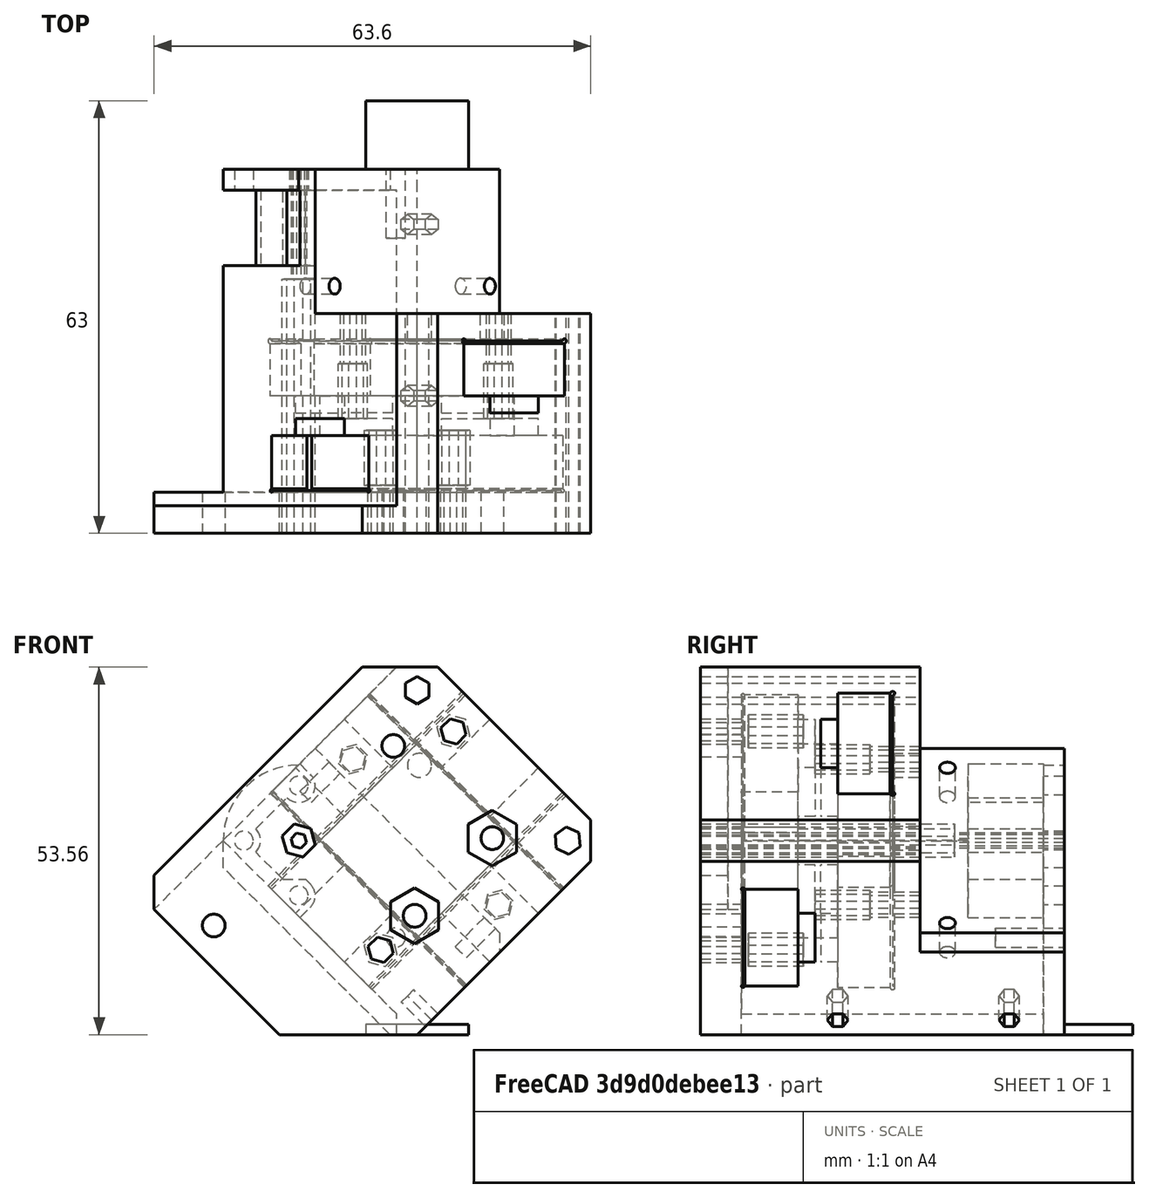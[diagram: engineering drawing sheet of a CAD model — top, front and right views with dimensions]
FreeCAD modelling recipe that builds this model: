
FCSTD DOCUMENT  (FreeCAD 0.19R)
Label: ToolHead_NoScreen_4PocketSplit2Bolts
License: All rights reserved
LicenseURL: http://en.wikipedia.org/wiki/All_rights_reserved
objects: Sketcher::SketchObject×34, PartDesign::Pocket×23, PartDesign::Pad×5, Mesh::Feature×3, PartDesign::Body×1
note: 91 computed .brp shape members not serialized (recipe doc carries the construction recipe); baked Part::Feature solids carry a one-line shape summary decoded from their .brp

FEATURE [Sketcher::SketchObject] Sketch  label="Body001"
  FullyConstrained = true
  MapMode = 5
  Support = -> [XY_Plane]
  sketch-geometry (11):
    g0: LineSegment StartX=20 StartY=15.7574 StartZ=0 EndX=20 EndY=-15.7574 EndZ=0
    g1: LineSegment StartX=15.7574 StartY=-20 StartZ=0 EndX=-20 EndY=-20 EndZ=0
    g2: LineSegment StartX=-20 StartY=-15.7574 StartZ=0 EndX=-20 EndY=19.9515 EndZ=0
    g3: Circle CenterX=-12.1976 CenterY=12.1976 CenterZ=0 NormalX=0 NormalY=0 NormalZ=1 AngleXU=0 Radius=2.1
    g4: LineSegment StartX=-12.1976 StartY=12.1976 StartZ=0 EndX=0 EndY=0 EndZ=0
    g5: ArcOfCircle CenterX=-12.1976 CenterY=12.1976 CenterZ=0 NormalX=0 NormalY=0 NormalZ=1 AngleXU=0 Radius=11 StartAngle=0.788519 EndAngle=2.35931
    g6: LineSegment StartX=-4.44373 StartY=20 StartZ=0 EndX=15.7574 EndY=20 EndZ=0
    g7: LineSegment StartX=15.7574 StartY=-20 StartZ=0 EndX=20 EndY=-15.7574 EndZ=0
    g8: LineSegment StartX=-20 StartY=-15.7574 StartZ=0 EndX=-22.1213 EndY=-17.8787 EndZ=0
    g9: LineSegment StartX=-22.1213 StartY=-17.8787 StartZ=0 EndX=-20 EndY=-20 EndZ=0
    g10: LineSegment StartX=15.7574 StartY=20 StartZ=0 EndX=20 EndY=15.7574 EndZ=0
  constraints (32):
    c: Horizontal(g1)
    c: Vertical(g0)
    c: Vertical(g2)
    c: Distance(g-1,g3) = 17.25
    c: Coincident(g4,g3)
    c: Coincident(g4,g-1)
    c: Angle(g4) = -0.785398
    c: Diameter(g3) = 4.2
    c: Coincident(g5,g3)
    c: Diameter(g5) = 22
    c: DistanceX(g1) = -20
    c: Coincident(g6,g5)
    c: Horizontal(g6)
    c: Coincident(g5,g2)
    c: Coincident(g7,g1)
    c: Coincident(g7,g0)
    c: Angle(g7) = 0.785398
    c: Distance(g7) = 6
    c: DistanceY(g1) = -20
    c: Coincident(g2,g8)
    c: Coincident(g8,g9)
    c: Coincident(g9,g1)
    c: Angle(g9) = -0.785398
    c: Angle(g8) = -2.35619
    c: Distance(g9) = 3
    c: DistanceX(g2) = -20
    c: Coincident(g10,g6)
    c: Coincident(g10,g0)
    c: Distance(g10) = 6
    c: Angle(g10) = -0.785398
    c: DistanceX(g0) = 20
    c: DistanceY(g6) = 20
FEATURE [PartDesign::Pad] Pad
  Direction = (1,1,1)
  Length = 53
  Length2 = 10
  Profile = -> Sketch
  Reversed = true
  Type = 0
FEATURE [Sketcher::SketchObject] Sketch001  label="RailHole"
  FullyConstrained = true
  MapMode = 5
  Placement = pos=(20,0,0) rot=(0.57735,0.57735,0.57735;2.0944rad)
  Support = -> [Pad]
  sketch-geometry (10):
    g0: LineSegment StartX=-10.35 StartY=-27.65 StartZ=0 EndX=-10.35 EndY=-20 EndZ=0
    g1: LineSegment StartX=5 StartY=-17.5 StartZ=0 EndX=-5 EndY=-17.5 EndZ=0
    g2: LineSegment StartX=10 StartY=-28 StartZ=0 EndX=-10 EndY=-28 EndZ=0
    g3: LineSegment StartX=5 StartY=-17.5 StartZ=0 EndX=5 EndY=-20 EndZ=0
    g4: LineSegment StartX=-5 StartY=-20 StartZ=0 EndX=-5 EndY=-17.5 EndZ=0
    g5: LineSegment StartX=-10.35 StartY=-20 StartZ=0 EndX=-5 EndY=-20 EndZ=0
    g6: LineSegment StartX=5 StartY=-20 StartZ=0 EndX=10.3495 EndY=-20 EndZ=0
    g7: LineSegment StartX=10.3495 StartY=-27.65 StartZ=0 EndX=10.3495 EndY=-20 EndZ=0
    g8: ArcOfCircle CenterX=-10.35 CenterY=-28 CenterZ=0 NormalX=0 NormalY=0 NormalZ=1 AngleXU=0 Radius=0.35 StartAngle=1.5708 EndAngle=6.28319
    g9: ArcOfCircle CenterX=10.35 CenterY=-28 CenterZ=0 NormalX=0 NormalY=0 NormalZ=1 AngleXU=0 Radius=0.35 StartAngle=3.14159 EndAngle=7.85541
  constraints (29):
    c: Vertical(g0)
    c: Symmetric(g1,g1,g-2)
    c: Distance(g1) = 10
    c: Coincident(g1,g3)
    c: Vertical(g3)
    c: Coincident(g4,g1)
    c: Symmetric(g3,g4,g-2)
    c: Distance(g3) = 2.5
    c: Distance(g2) = 20
    c: Coincident(g5,g4)
    c: Horizontal(g5)
    c: Coincident(g3,g6)
    c: Horizontal(g6)
    c: Vertical(g7)
    c: Coincident(g0,g5)
    c: Coincident(g7,g6)
    c: Coincident(g0,g8)
    c: Coincident(g8,g2)
    c: Diameter(g8) = 0.7
    c: DistanceX(g0,g8) = 0
    c: DistanceY(g2,g8) = 0
    c: Coincident(g9,g2)
    c: Coincident(g9,g7)
    c: Diameter(g9) = 0.7
    c: DistanceY(g2,g9) = 0
    c: DistanceX(g7,g9) = 0.0005
    c: Symmetric(g9,g8,g-2)
    c: Distance(g9,g6) = 8
    c: DistanceY(g8) = -28
FEATURE [PartDesign::Pocket] Pocket
  BaseFeature = -> Pad
  Length = 5
  Length2 = 100
  Profile = -> Sketch001
  Type = 1
FEATURE [Sketcher::SketchObject] Sketch008  label="ExtruderHole"
  FullyConstrained = false
  MapMode = 5
  Placement = pos=(0,0,4) rot=(0,0,1;0rad)
  sketch-geometry (2):
    g0: LineSegment StartX=0 StartY=0 StartZ=0 EndX=-54.6242 EndY=54.6242 EndZ=0
    g1: Circle CenterX=-12.1976 CenterY=12.1976 CenterZ=0 NormalX=0 NormalY=0 NormalZ=1 AngleXU=0 Radius=0.75
  constraints (5):
    c: Coincident(g0,g-1)
    c: Angle(g0) = 2.35619
    c: PointOnObject(g1,g0)
    c: Distance(g-1,g1) = 17.25
    c: Diameter(g1) = 1.5
FEATURE [Sketcher::SketchObject] Sketch009  label="reference"
  FullyConstrained = false
  MapMode = 5
  Placement = pos=(0,0,-25) rot=(1,0,0;3.14159rad)
  sketch-geometry (2):
    g0: Circle CenterX=-12.0208 CenterY=-12.0208 CenterZ=0 NormalX=0 NormalY=0 NormalZ=1 AngleXU=0 Radius=10
    g1: LineSegment StartX=0 StartY=0 StartZ=0 EndX=-27.7674 EndY=-27.7674 EndZ=0
  constraints (5):
    c: Diameter(g0) = 20
    c: Coincident(g1,g-1)
    c: Angle(g1) = -2.35619
    c: PointOnObject(g0,g1)
    c: Distance(g0,g1) = 17
FEATURE [Sketcher::SketchObject] Sketch010  label="reference2"
  FullyConstrained = false
  MapMode = 5
  Placement = pos=(0,0,-37) rot=(1,0,0;3.14159rad)
  sketch-geometry (2):
    g0: Circle CenterX=-12.1976 CenterY=-12.1976 CenterZ=0 NormalX=0 NormalY=0 NormalZ=1 AngleXU=0 Radius=8
    g1: LineSegment StartX=0 StartY=0 StartZ=0 EndX=-38.1566 EndY=-38.1566 EndZ=0
  constraints (5):
    c: Diameter(g0) = 16
    c: Coincident(g1,g-1)
    c: Angle(g1) = -2.35619
    c: Distance(g0,g1) = 17.25
    c: PointOnObject(g0,g1)
FEATURE [Sketcher::SketchObject] Sketch021  label="InternalTri"
  FullyConstrained = true
  MapMode = 5
  Placement = pos=(0,-3e-15,-12) rot=(0,0,1;0rad)
  sketch-geometry (4):
    g0: LineSegment StartX=-10 StartY=10 StartZ=0 EndX=10 EndY=10 EndZ=0
    g1: LineSegment StartX=10 StartY=10 StartZ=0 EndX=10 EndY=-10 EndZ=0
    g2: LineSegment StartX=10 StartY=-10 StartZ=0 EndX=-10 EndY=-10 EndZ=0
    g3: LineSegment StartX=-10 StartY=-10 StartZ=0 EndX=-10 EndY=10 EndZ=0
  constraints (11):
    c: Coincident(g0,g1)
    c: Coincident(g1,g2)
    c: Coincident(g2,g3)
    c: Coincident(g3,g0)
    c: Horizontal(g0)
    c: Horizontal(g2)
    c: Vertical(g1)
    c: Vertical(g3)
    c: Symmetric(g1,g0,g-1)
    c: Equal(g1,g0)
    c: Distance(g1) = 20
FEATURE [PartDesign::Pocket] Pocket002
  BaseFeature = -> Pocket
  Length = 10
  Length2 = 2
  Profile = -> Sketch021
  Type = 4
FEATURE [Sketcher::SketchObject] Sketch019  label="RailHole2"
  FullyConstrained = true
  MapMode = 5
  Placement = pos=(0,-20,0) rot=(1,0,0;1.5708rad)
  Support = -> [Pocket002]
  sketch-geometry (10):
    g0: LineSegment StartX=-9.75 StartY=-6.2 StartZ=0 EndX=9.75 EndY=-6.2 EndZ=0
    g1: LineSegment StartX=10 StartY=-14.2 StartZ=0 EndX=5 EndY=-14.2 EndZ=0
    g2: LineSegment StartX=5 StartY=-14.2 StartZ=0 EndX=5 EndY=-16.7 EndZ=0
    g3: LineSegment StartX=5 StartY=-16.7 StartZ=0 EndX=-5 EndY=-16.7 EndZ=0
    g4: LineSegment StartX=-5 StartY=-16.7 StartZ=0 EndX=-5 EndY=-14.2 EndZ=0
    g5: LineSegment StartX=-5 StartY=-14.2 StartZ=0 EndX=-10 EndY=-14.2 EndZ=0
    g6: ArcOfCircle CenterX=10 CenterY=-6.2 CenterZ=0 NormalX=0 NormalY=0 NormalZ=1 AngleXU=0 Radius=0.25 StartAngle=4.71239 EndAngle=9.42478
    g7: ArcOfCircle CenterX=-10 CenterY=-6.2 CenterZ=0 NormalX=0 NormalY=0 NormalZ=1 AngleXU=0 Radius=0.25 StartAngle=-9e-16 EndAngle=4.71239
    g8: LineSegment StartX=-10 StartY=-14.2 StartZ=0 EndX=-10 EndY=-6.45 EndZ=0
    g9: LineSegment StartX=10 StartY=-14.2 StartZ=0 EndX=10 EndY=-6.45 EndZ=0
  constraints (29):
    c: Horizontal(g0)
    c: Horizontal(g1)
    c: Coincident(g1,g2)
    c: Vertical(g2)
    c: Coincident(g2,g3)
    c: Horizontal(g3)
    c: Coincident(g3,g4)
    c: Vertical(g4)
    c: Coincident(g4,g5)
    c: Symmetric(g1,g5,g-2)
    c: Distance(g3) = 10
    c: Symmetric(g4,g1,g-2)
    c: DistanceY(g0) = -6.2
    c: Distance(g2) = 2.5
    c: Coincident(g6,g0)
    c: Coincident(g7,g0)
    c: Distance(g7,g6) = 20
    c: DistanceY(g1,g6) = 8
    c: Coincident(g8,g5)
    c: Vertical(g8)
    c: Coincident(g9,g1)
    c: Coincident(g9,g6)
    c: Vertical(g9)
    c: Coincident(g7,g8)
    c: Symmetric(g6,g7,g-2)
    c: Diameter(g6) = 0.5
    c: Equal(g6,g7)
    c: DistanceX(g7,g7) = 0
    c: DistanceY(g7,g0) = 0
FEATURE [Sketcher::SketchObject] Sketch024  label="hgxLITEholes"
  FullyConstrained = false
  MapMode = 5
  Placement = pos=(0,0,4) rot=(0,0,1;0rad)
  sketch-geometry (5):
    g0: Circle CenterX=7.3 CenterY=12.2 CenterZ=0 NormalX=0 NormalY=0 NormalZ=1 AngleXU=0 Radius=1.65
    g1: Circle CenterX=-29.7 CenterY=12.2 CenterZ=0 NormalX=0 NormalY=0 NormalZ=1 AngleXU=0 Radius=1.65
    g2: LineSegment StartX=-29.7 StartY=12.2 StartZ=0 EndX=7.3 EndY=12.2 EndZ=0
    g3: LineSegment StartX=0 StartY=0 StartZ=0 EndX=-27.1729 EndY=27.1729 EndZ=0
    g4: Circle CenterX=-12.2 CenterY=12.2 CenterZ=0 NormalX=0 NormalY=0 NormalZ=1 AngleXU=0 Radius=1.0154
  constraints (12):
    c: Diameter(g0) = 3.3
    c: Equal(g0,g1)
    c: Coincident(g2,g1)
    c: Coincident(g2,g0)
    c: Distance(g2) = 37
    c: Coincident(g3,g-1)
    c: Angle(g3) = 2.35619
    c: PointOnObject(g4,g3)
    c: Distance(g4,g0) = 19.5
    c: Horizontal(g2)
    c: PointOnObject(g4,g2)
    c: DistanceY(g4) = 12.2
FEATURE [PartDesign::Pocket] Pocket003
  BaseFeature = -> Pocket002
  Length = 5
  Length2 = 100
  Profile = -> Sketch019
  Type = 1
FEATURE [Sketcher::SketchObject] Sketch026  label="BottomSculp"
  FullyConstrained = false
  MapMode = 5
  Placement = pos=(0,0,-53) rot=(1,0,0;3.14159rad)
  Support = -> [Pocket003]
  sketch-geometry (5):
    g0: LineSegment StartX=29.4648 StartY=27.8981 StartZ=0 EndX=28.2209 EndY=-23.4245 EndZ=0
    g1: LineSegment StartX=28.2209 StartY=-23.4245 StartZ=0 EndX=-1.00001 EndY=-23.4245 EndZ=0
    g2: LineSegment StartX=-1.00001 StartY=-23.4245 StartZ=0 EndX=-1 EndY=18 EndZ=0
    g3: LineSegment StartX=-1 StartY=18 StartZ=0 EndX=-14.2089 EndY=31.2089 EndZ=0
    g4: LineSegment StartX=-14.2089 StartY=31.2089 StartZ=0 EndX=29.4648 EndY=27.8981 EndZ=0
  constraints (11):
    c: Coincident(g0,g1)
    c: Horizontal(g1)
    c: Coincident(g1,g2)
    c: Angle(g2) = 1.5708
    c: Coincident(g2,g3)
    c: Angle(g3) = 2.35619
    c: Coincident(g4,g3)
    c: Coincident(g4,g0)
    c: DistanceY(g2) = 18
    c: DistanceX(g2) = -1
    c: Angle(g3) = 2.35619
FEATURE [PartDesign::Pocket] Pocket004
  BaseFeature = -> Pocket003
  Length = 21
  Length2 = 100
  Profile = -> Sketch026
  Type = 0
FEATURE [Sketcher::SketchObject] Sketch004  label="Yboltpattern"
  FullyConstrained = true
  MapMode = 5
  Placement = pos=(0,0,-32) rot=(1,0,0;3.14159rad)
  Support = -> [Pocket004]
  sketch-geometry (8):
    g0: Circle CenterX=-8 CenterY=7.5 CenterZ=0 NormalX=0 NormalY=0 NormalZ=1 AngleXU=0 Radius=1.75
    g1: Circle CenterX=8 CenterY=7.5 CenterZ=0 NormalX=0 NormalY=0 NormalZ=1 AngleXU=0 Radius=1.75
    g2: Circle CenterX=-8 CenterY=-7.5 CenterZ=0 NormalX=0 NormalY=0 NormalZ=1 AngleXU=0 Radius=1.75
    g3: Circle CenterX=8 CenterY=-7.5 CenterZ=0 NormalX=0 NormalY=0 NormalZ=1 AngleXU=0 Radius=1.75
    g4: LineSegment StartX=-8 StartY=7.5 StartZ=0 EndX=8 EndY=7.5 EndZ=0
    g5: LineSegment StartX=8 StartY=7.5 StartZ=0 EndX=8 EndY=-7.5 EndZ=0
    g6: LineSegment StartX=8 StartY=-7.5 StartZ=0 EndX=-8 EndY=-7.5 EndZ=0
    g7: LineSegment StartX=-8 StartY=-7.5 StartZ=0 EndX=-8 EndY=7.5 EndZ=0
  constraints (18):
    c: Diameter(g0) = 3.5
    c: Equal(g0,g1)
    c: Equal(g0,g2)
    c: Equal(g0,g3)
    c: Distance(g2,g0) = 15
    c: Distance(g3,g2) = 16
    c: Coincident(g4,g0)
    c: Coincident(g4,g1)
    c: Coincident(g4,g5)
    c: Coincident(g5,g3)
    c: Coincident(g5,g6)
    c: Coincident(g6,g2)
    c: Coincident(g6,g7)
    c: Coincident(g7,g4)
    c: Equal(g5,g7)
    c: Equal(g4,g6)
    c: Symmetric(g1,g2,g-1)
    c: Symmetric(g0,g1,g-2)
FEATURE [Sketcher::SketchObject] Sketch022  label="VoronHoleRelif"
  FullyConstrained = true
  MapMode = 5
  Placement = pos=(0,0,-28) rot=(0,0,1;0rad)
  Support = -> [Pocket004]
  sketch-geometry (11):
    g0: ArcOfCircle CenterX=-17.8884 CenterY=6.52425 CenterZ=0 NormalX=0 NormalY=0 NormalZ=1 AngleXU=0 Radius=2.4 StartAngle=4.71239 EndAngle=6.28319
    g1: ArcOfCircle CenterX=-6.58192 CenterY=17.8307 CenterZ=0 NormalX=0 NormalY=0 NormalZ=1 AngleXU=0 Radius=2.4 StartAngle=3.14159 EndAngle=6.28319
    g2: LineSegment StartX=-22.2684 StartY=4.12425 StartZ=0 EndX=-17.8884 EndY=4.12425 EndZ=0
    g3: LineSegment StartX=-22.2684 StartY=23.8307 StartZ=0 EndX=-4.18192 EndY=23.8307 EndZ=0
    g4: LineSegment StartX=-4.18192 StartY=23.8307 StartZ=0 EndX=-4.18192 EndY=17.8307 EndZ=0
    g5: LineSegment StartX=-22.2684 StartY=4.12425 StartZ=0 EndX=-22.2684 EndY=23.8307 EndZ=0
    g6: ArcOfCircle CenterX=-17.8172 CenterY=17.8307 CenterZ=0 NormalX=0 NormalY=0 NormalZ=1 AngleXU=0 Radius=2.4 StartAngle=4.71239 EndAngle=6.28319
    g7: LineSegment StartX=-15.4172 StartY=17.8307 StartZ=0 EndX=-8.98192 EndY=17.8307 EndZ=0
    g8: LineSegment StartX=-17.8172 StartY=9.85307 StartZ=0 EndX=-15.4884 EndY=7.52425 EndZ=0
    g9: LineSegment StartX=-15.4884 StartY=6.52425 StartZ=0 EndX=-15.4884 EndY=7.52425 EndZ=0
    g10: LineSegment StartX=-17.8172 StartY=9.85307 StartZ=0 EndX=-17.8172 EndY=15.4307 EndZ=0
  constraints (33):
    c: Horizontal(g2)
    c: Coincident(g3,g4)
    c: Tangent(g4,g1) = 1.5708
    c: Tangent(g2,g0) = -1.5708
    c: Diameter(g0) = 4.8
    c: Equal(g0,g1)
    c: Vertical(g4)
    c: Horizontal(g3)
    c: Coincident(g5,g2)
    c: Coincident(g5,g3)
    c: Vertical(g5)
    c: Distance(g2) = 4.38
    c: Distance(g4) = 6
    c: DistanceX(g1) = -6.58192
    c: DistanceY(g1) = 17.8307
    c: DistanceX(g0) = -17.8884
    c: DistanceY(g0) = 6.52425
    c: Coincident(g7,g6)
    c: Coincident(g7,g1)
    c: Horizontal(g7)
    c: Perpendicular(g1,g7)
    c: Diameter(g6) = 4.8
    c: Perpendicular(g6,g7)
    c: Angle(g8) = -0.785398
    c: Vertical(g9)
    c: Tangent(g9,g0) = -1.5708
    c: Distance(g9) = 1
    c: Coincident(g8,g9)
    c: Coincident(g10,g8)
    c: Coincident(g10,g6)
    c: Vertical(g10)
    c: Perpendicular(g6,g10)
    c: DistanceX(g6) = -17.8172
FEATURE [PartDesign::Pocket] Pocket005
  BaseFeature = -> Pocket004
  Length = 22
  Length2 = -11
  Profile = -> Sketch022
  Type = 4
FEATURE [Sketcher::SketchObject] Sketch017  label="VoronHoles3"
  FullyConstrained = true
  MapMode = 5
  Placement = pos=(0,0,-50) rot=(0,0,1;0rad)
  Support = -> [Pocket005]
  sketch-geometry (10):
    g0: Circle CenterX=-6.54074 CenterY=17.8544 CenterZ=0 NormalX=0 NormalY=0 NormalZ=1 AngleXU=0 Radius=1.375
    g1: Circle CenterX=-17.8544 CenterY=6.54074 CenterZ=0 NormalX=0 NormalY=0 NormalZ=1 AngleXU=0 Radius=1.375
    g2: Circle CenterX=-6.54074 CenterY=6.54074 CenterZ=0 NormalX=0 NormalY=0 NormalZ=1 AngleXU=0 Radius=1.375
    g3: Circle CenterX=-17.8544 CenterY=17.8544 CenterZ=0 NormalX=0 NormalY=0 NormalZ=1 AngleXU=0 Radius=1.375
    g4: LineSegment StartX=-6.54074 StartY=17.8544 StartZ=0 EndX=-6.54074 EndY=6.54074 EndZ=0
    g5: LineSegment StartX=-6.54074 StartY=6.54074 StartZ=0 EndX=-17.8544 EndY=6.54074 EndZ=0
    g6: LineSegment StartX=-17.8544 StartY=6.54074 StartZ=0 EndX=-17.8544 EndY=17.8544 EndZ=0
    g7: LineSegment StartX=-17.8544 StartY=17.8544 StartZ=0 EndX=-6.54074 EndY=17.8544 EndZ=0
    g8: LineSegment StartX=0 StartY=0 StartZ=0 EndX=-37.1726 EndY=37.1726 EndZ=0
    g9: Circle CenterX=-12.1976 CenterY=12.1976 CenterZ=0 NormalX=0 NormalY=0 NormalZ=1 AngleXU=0 Radius=0.77
  constraints (25):
    c: Coincident(g4,g0)
    c: Coincident(g4,g2)
    c: Coincident(g4,g5)
    c: Coincident(g5,g1)
    c: Coincident(g5,g6)
    c: Coincident(g6,g3)
    c: Coincident(g6,g7)
    c: Coincident(g7,g4)
    c: Equal(g4,g7)
    c: Equal(g7,g6)
    c: Equal(g6,g5)
    c: Coincident(g8,g-1)
    c: PointOnObject(g9,g8)
    c: Distance(g-1,g9) = 17.25
    c: Diameter(g1) = 2.75
    c: Equal(g1,g3)
    c: Equal(g1,g0)
    c: Equal(g1,g2)
    c: Symmetric(g0,g1,g9)
    c: Distance(g2,g3) = 16
    c: Angle(g8) = 2.35619
    c: PointOnObject(g2,g8)
    c: Perpendicular(g7,g4)
    c: Distance(g8) = 52.57
    c: Diameter(g9) = 1.54
FEATURE [PartDesign::Pocket] Pocket006
  BaseFeature = -> Pocket005
  Length = 5
  Length2 = 100
  Profile = -> Sketch017
  Type = 1
FEATURE [Sketcher::SketchObject] Sketch025  label="FanDuctMountHole"
  FullyConstrained = true
  MapMode = 5
  Placement = pos=(0,0,-53) rot=(1,0,0;3.14159rad)
  Support = -> [Pocket006]
  sketch-geometry (1):
    g0: Circle CenterX=-12.2 CenterY=7.8 CenterZ=0 NormalX=0 NormalY=0 NormalZ=1 AngleXU=0 Radius=1.4
  constraints (3):
    c: Diameter(g0) = 2.8
    c: DistanceX(g0) = -12.2
    c: DistanceY(g0) = 7.8
FEATURE [PartDesign::Pocket] Pocket007
  BaseFeature = -> Pocket006
  Length = 10
  Length2 = 100
  Profile = -> Sketch025
  Type = 0
FEATURE [PartDesign::Pocket] Pocket008
  BaseFeature = -> Pocket007
  Length = 9
  Length2 = 100
  Profile = -> Sketch004
  Type = 0
FEATURE [Sketcher::SketchObject] Sketch007  label="ExtruderPlatform"
  ExternalGeometry = -> [Pad]
  FullyConstrained = false
  MapMode = 5
  Support = -> [Pocket008]
  sketch-geometry (12):
    g0: LineSegment StartX=-20 StartY=-20 StartZ=0 EndX=15.7574 EndY=-20 EndZ=0
    g1: LineSegment StartX=0 StartY=0 StartZ=0 EndX=-70.7107 EndY=70.7107 EndZ=0
    g2: Circle CenterX=-12.1976 CenterY=12.1976 CenterZ=0 NormalX=0 NormalY=0 NormalZ=1 AngleXU=0 Radius=2.125
    g3: LineSegment StartX=15.7574 StartY=-20 StartZ=0 EndX=20 EndY=-15.7574 EndZ=0
    g4: LineSegment StartX=20 StartY=-15.7574 StartZ=0 EndX=20 EndY=15.7574 EndZ=0
    g5: LineSegment StartX=20 StartY=15.7574 StartZ=0 EndX=15.7574 EndY=20 EndZ=0
    g6: LineSegment StartX=-20 StartY=-20 StartZ=0 EndX=-34.1976 EndY=-5.80241 EndZ=0
    g7: LineSegment StartX=-12.1976 StartY=-100 StartZ=0 EndX=-12.1976 EndY=100 EndZ=0
    g8: LineSegment StartX=-34.1976 StartY=-5.80241 StartZ=0 EndX=-34.1976 EndY=20 EndZ=0
    g9: LineSegment StartX=-34.1976 StartY=20 StartZ=0 EndX=15.7574 EndY=20 EndZ=0
    g10: Circle CenterX=-29.6976 CenterY=12.1976 CenterZ=0 NormalX=0 NormalY=0 NormalZ=1 AngleXU=0 Radius=1.4
    g11: Circle CenterX=7.30241 CenterY=11.9057 CenterZ=0 NormalX=0 NormalY=0 NormalZ=1 AngleXU=0 Radius=1.4
  constraints (35):
    c: Coincident(g1,g-1)
    c: Angle(g1) = 2.35619
    c: Diameter(g2) = 4.25
    c: PointOnObject(g2,g1)
    c: Distance(g-1,g2) = 17.25
    c: Coincident(g0,g3)
    c: Coincident(g3,g4)
    c: Coincident(g6,g0)
    c: Angle(g6) = 2.35619
    c: Coincident(g5,g4)
    c: Distance(g1) = 100
    c: PointOnObject(g2,g7)
    c: DistanceX(g0,g0) = -35.7574
    c: DistanceY(g0,g0) = 0
    c: DistanceX(g3,g0) = -40
    c: DistanceY(g3,g0) = -4.24264
    c: DistanceX(g4) = 20
    c: DistanceY(g4) = 15.7574
    c: DistanceX(g3) = 20
    c: DistanceY(g3) = -15.7574
    c: Coincident(g8,g6)
    c: Vertical(g8)
    c: Horizontal(g9)
    c: Coincident(g5,g9)
    c: Distance(g8,g7) = 22
    c: DistanceX(g5) = 15.7574
    c: DistanceY(g5) = 20
    c: Symmetric(g7,g7,g-1)
    c: Distance(g7) = 200
    c: DistanceX(g10,g2) = 17.5
    c: DistanceX(g2,g11) = 19.5
    c: Diameter(g10) = 2.8
    c: Equal(g10,g11)
    c: DistanceY(g10,g2) = 0
    c: Coincident(g9,g8)
FEATURE [PartDesign::Pad] Pad001
  BaseFeature = -> Pocket008
  Direction = (1,1,1)
  Length = 6
  Length2 = 100
  Profile = -> Sketch007
  Reversed = true
  Type = 0
FEATURE [PartDesign::Pocket] Pocket009
  BaseFeature = -> Pad001
  Length = 11
  Length2 = 100
  Profile = -> Sketch024
  Type = 0
FEATURE [PartDesign::Pocket] Pocket010
  BaseFeature = -> Pocket009
  Length = 5
  Length2 = 100
  Profile = -> Sketch008
  Type = 1
FEATURE [Sketcher::SketchObject] Sketch003  label="Xboltpattern"
  FullyConstrained = true
  MapMode = 5
  Support = -> [Pocket010]
  sketch-geometry (8):
    g0: Circle CenterX=-8 CenterY=7.5 CenterZ=0 NormalX=0 NormalY=0 NormalZ=1 AngleXU=0 Radius=1.65
    g1: Circle CenterX=8 CenterY=7.5 CenterZ=0 NormalX=0 NormalY=0 NormalZ=1 AngleXU=0 Radius=1.65
    g2: Circle CenterX=-8 CenterY=-7.5 CenterZ=0 NormalX=0 NormalY=0 NormalZ=1 AngleXU=0 Radius=1.65
    g3: Circle CenterX=8 CenterY=-7.5 CenterZ=0 NormalX=0 NormalY=0 NormalZ=1 AngleXU=0 Radius=1.65
    g4: LineSegment StartX=-8 StartY=7.5 StartZ=0 EndX=8 EndY=7.5 EndZ=0
    g5: LineSegment StartX=8 StartY=7.5 StartZ=0 EndX=8 EndY=-7.5 EndZ=0
    g6: LineSegment StartX=8 StartY=-7.5 StartZ=0 EndX=-8 EndY=-7.5 EndZ=0
    g7: LineSegment StartX=-8 StartY=-7.5 StartZ=0 EndX=-8 EndY=7.5 EndZ=0
  constraints (19):
    c: Diameter(g0) = 3.3
    c: Equal(g0,g1)
    c: Equal(g0,g2)
    c: Equal(g0,g3)
    c: Distance(g0,g1) = 16
    c: Distance(g1,g3) = 15
    c: Coincident(g4,g0)
    c: Coincident(g4,g1)
    c: Horizontal(g4)
    c: Coincident(g4,g5)
    c: Coincident(g5,g3)
    c: Vertical(g5)
    c: Coincident(g5,g6)
    c: Coincident(g6,g2)
    c: Coincident(g6,g7)
    c: Coincident(g7,g4)
    c: Symmetric(g2,g1,g-1)
    c: Equal(g7,g5)
    c: Equal(g6,g4)
FEATURE [Sketcher::SketchObject] Sketch029  label="Adhesion"
  FullyConstrained = false
  MapMode = 5
  Placement = pos=(0,0,-53) rot=(1,0,0;3.14159rad)
  sketch-geometry (4):
    g0: LineSegment StartX=-13.636 StartY=24.2426 StartZ=0 EndX=-24.2426 EndY=13.636 EndZ=0
    g1: LineSegment StartX=-24.2426 StartY=13.636 StartZ=0 EndX=-25.3033 EndY=14.6967 EndZ=0
    g2: LineSegment StartX=-25.3033 StartY=14.6967 StartZ=0 EndX=-14.6967 EndY=25.3033 EndZ=0
    g3: LineSegment StartX=-14.6967 StartY=25.3033 StartZ=0 EndX=-13.636 EndY=24.2426 EndZ=0
  constraints (10):
    c: Coincident(g0,g1)
    c: Coincident(g1,g2)
    c: Coincident(g2,g3)
    c: Coincident(g3,g0)
    c: Angle(g2) = 0.785398
    c: Distance(g2) = 15
    c: Distance(g1) = 1.5
    c: Distance(g3) = 1.5
    c: Perpendicular(g2,g3)
    c: Perpendicular(g2,g1)
FEATURE [Sketcher::SketchObject] Sketch033  label="WireMgmnt"
  FullyConstrained = true
  MapMode = 5
  Placement = pos=(0,-20,0) rot=(1,0,0;1.5708rad)
  sketch-geometry (14):
    g0: LineSegment StartX=-15.7 StartY=-20.7506 StartZ=0 EndX=-15.7 EndY=-19.2494 EndZ=0
    g1: LineSegment StartX=-15.7 StartY=-19.2494 StartZ=0 EndX=-17 EndY=-18.4989 EndZ=0
    g2: LineSegment StartX=-17 StartY=-18.4989 StartZ=0 EndX=-18.3 EndY=-19.2494 EndZ=0
    g3: LineSegment StartX=-18.3 StartY=-19.2494 StartZ=0 EndX=-18.3 EndY=-20.7506 EndZ=0
    g4: LineSegment StartX=-18.3 StartY=-20.7506 StartZ=0 EndX=-17 EndY=-21.5011 EndZ=0
    g5: LineSegment StartX=-17 StartY=-21.5011 StartZ=0 EndX=-15.7 EndY=-20.7506 EndZ=0
    g6: Circle CenterX=-17 CenterY=-20 CenterZ=0 NormalX=0 NormalY=0 NormalZ=1 AngleXU=0 Radius=1.50111
    g7: LineSegment StartX=-15.7 StartY=-44.2494 StartZ=0 EndX=-17 EndY=-43.4989 EndZ=0
    g8: LineSegment StartX=-17 StartY=-43.4989 StartZ=0 EndX=-18.3 EndY=-44.2494 EndZ=0
    g9: LineSegment StartX=-18.3 StartY=-44.2494 StartZ=0 EndX=-18.3 EndY=-45.7506 EndZ=0
    g10: LineSegment StartX=-18.3 StartY=-45.7506 StartZ=0 EndX=-17 EndY=-46.5011 EndZ=0
    g11: LineSegment StartX=-17 StartY=-46.5011 StartZ=0 EndX=-15.7 EndY=-45.7506 EndZ=0
    g12: LineSegment StartX=-15.7 StartY=-45.7506 StartZ=0 EndX=-15.7 EndY=-44.2494 EndZ=0
    g13: Circle CenterX=-17 CenterY=-45 CenterZ=0 NormalX=0 NormalY=0 NormalZ=1 AngleXU=0 Radius=1.50111
  constraints (34):
    c: Coincident(g0,g1)
    c: Coincident(g1,g2)
    c: Coincident(g2,g3)
    c: Coincident(g3,g4)
    c: Coincident(g4,g5)
    c: Coincident(g5,g0)
    c: Equal(g0, g1-g5) x5
    c: PointOnObject(g0,g6)
    c: PointOnObject(g1,g6)
    c: PointOnObject(g2,g6)
    c: PointOnObject(g3,g6)
    c: PointOnObject(g4,g6)
    c: PointOnObject(g5,g6)
    c: Coincident(g7,g8)
    c: Coincident(g8,g9)
    c: Coincident(g9,g10)
    c: Coincident(g10,g11)
    c: Coincident(g11,g12)
    c: Coincident(g12,g7)
    c: Equal(g7, g8-g12) x5
    c: PointOnObject(g7,g13)
    c: PointOnObject(g8,g13)
    c: PointOnObject(g9,g13)
    c: PointOnObject(g10,g13)
    c: PointOnObject(g11,g13)
    c: PointOnObject(g12,g13)
    c: DistanceX(g13) = -17
    c: Distance(g10,g7) = 2.6
    c: Vertical(g9)
    c: DistanceY(g13) = -45
    c: Distance(g3,g0) = 2.6
    c: DistanceY(g6) = -20
    c: Vertical(g3)
    c: DistanceX(g6) = -17
FEATURE [Sketcher::SketchObject] Sketch035  label="Bottom Reinforce"
  FullyConstrained = false
  MapMode = 5
  Placement = pos=(0,0,-53) rot=(1,0,0;3.14159rad)
  sketch-geometry (4):
    g0: LineSegment StartX=-22.779 StartY=17.221 StartZ=0 EndX=-22.779 EndY=-17.1725 EndZ=0
    g1: LineSegment StartX=-22.779 StartY=-17.1725 StartZ=0 EndX=-20 EndY=-19.9515 EndZ=0
    g2: LineSegment StartX=-20 StartY=-19.9515 StartZ=0 EndX=-20 EndY=20 EndZ=0
    g3: LineSegment StartX=-20 StartY=20 StartZ=0 EndX=-22.779 EndY=17.221 EndZ=0
  constraints (9):
    c: Vertical(g0)
    c: Coincident(g0,g1)
    c: Coincident(g1,g2)
    c: Vertical(g2)
    c: Coincident(g2,g3)
    c: Coincident(g3,g0)
    c: Angle(g1) = -0.785398
    c: DistanceY(g2) = 20
    c: Angle(g3) = -2.35619
FEATURE [Sketcher::SketchObject] Sketch037  label="BumpTrim"
  FullyConstrained = false
  MapMode = 5
  sketch-geometry (4):
    g0: LineSegment StartX=-26.2848 StartY=31.2083 StartZ=0 EndX=-1.26106 EndY=31.2083 EndZ=0
    g1: LineSegment StartX=-1.26106 StartY=31.2083 StartZ=0 EndX=-1.26106 EndY=20 EndZ=0
    g2: LineSegment StartX=-1.26106 StartY=20 StartZ=0 EndX=-26.2848 EndY=20 EndZ=0
    g3: LineSegment StartX=-26.2848 StartY=20 StartZ=0 EndX=-26.2848 EndY=31.2083 EndZ=0
  constraints (9):
    c: Coincident(g0,g1)
    c: Coincident(g1,g2)
    c: Coincident(g2,g3)
    c: Coincident(g3,g0)
    c: Horizontal(g0)
    c: Horizontal(g2)
    c: Vertical(g1)
    c: Vertical(g3)
    c: DistanceY(g1) = 20
FEATURE [PartDesign::Pocket] Pocket011
  BaseFeature = -> Pocket010
  Length = 10
  Length2 = 100
  Profile = -> Sketch003
  Type = 0
FEATURE [Sketcher::SketchObject] Sketch036  label="countersink"
  FullyConstrained = true
  MapMode = 5
  Support = -> [Pocket011]
  sketch-geometry (14):
    g0: LineSegment StartX=11.9037 StartY=-8.546 StartZ=0 EndX=10.8577 EndY=-4.64226 EndZ=0
    g1: LineSegment StartX=10.8577 StartY=-4.64226 StartZ=0 EndX=6.954 EndY=-3.59626 EndZ=0
    g2: LineSegment StartX=6.954 StartY=-3.59626 StartZ=0 EndX=4.09626 EndY=-6.454 EndZ=0
    g3: LineSegment StartX=4.09626 StartY=-6.454 StartZ=0 EndX=5.14226 EndY=-10.3577 EndZ=0
    g4: LineSegment StartX=5.14226 StartY=-10.3577 StartZ=0 EndX=9.046 EndY=-11.4037 EndZ=0
    g5: LineSegment StartX=9.046 StartY=-11.4037 StartZ=0 EndX=11.9037 EndY=-8.546 EndZ=0
    g6: Circle CenterX=8 CenterY=-7.5 CenterZ=0 NormalX=0 NormalY=0 NormalZ=1 AngleXU=0 Radius=4.04145
    g7: LineSegment StartX=-5.14226 StartY=-4.64226 StartZ=0 EndX=-9.046 EndY=-3.59626 EndZ=0
    g8: LineSegment StartX=-9.046 StartY=-3.59626 StartZ=0 EndX=-11.9037 EndY=-6.454 EndZ=0
    g9: LineSegment StartX=-11.9037 StartY=-6.454 StartZ=0 EndX=-10.8577 EndY=-10.3577 EndZ=0
    g10: LineSegment StartX=-10.8577 StartY=-10.3577 StartZ=0 EndX=-6.954 EndY=-11.4037 EndZ=0
    g11: LineSegment StartX=-6.954 StartY=-11.4037 StartZ=0 EndX=-4.09626 EndY=-8.546 EndZ=0
    g12: LineSegment StartX=-4.09626 StartY=-8.546 StartZ=0 EndX=-5.14226 EndY=-4.64226 EndZ=0
    g13: Circle CenterX=-8 CenterY=-7.5 CenterZ=0 NormalX=0 NormalY=0 NormalZ=1 AngleXU=0 Radius=4.04145
  constraints (34):
    c: Coincident(g0,g1)
    c: Coincident(g1,g2)
    c: Coincident(g2,g3)
    c: Coincident(g3,g4)
    c: Coincident(g4,g5)
    c: Coincident(g5,g0)
    c: Equal(g0, g1-g5) x5
    c: PointOnObject(g0,g6)
    c: PointOnObject(g1,g6)
    c: PointOnObject(g2,g6)
    c: PointOnObject(g3,g6)
    c: PointOnObject(g4,g6)
    c: PointOnObject(g5,g6)
    c: Coincident(g7,g8)
    c: Coincident(g8,g9)
    c: Coincident(g9,g10)
    c: Coincident(g10,g11)
    c: Coincident(g11,g12)
    c: Coincident(g12,g7)
    c: Equal(g7, g8-g12) x5
    c: PointOnObject(g7,g13)
    c: PointOnObject(g8,g13)
    c: PointOnObject(g9,g13)
    c: PointOnObject(g10,g13)
    c: PointOnObject(g11,g13)
    c: PointOnObject(g12,g13)
    c: Angle(g11) = 0.785398
    c: Angle(g5) = 0.785398
    c: Distance(g0,g2) = 7
    c: Distance(g7,g8) = 7
    c: DistanceX(g6) = 8
    c: DistanceY(g6) = -7.5
    c: DistanceY(g13) = -7.5
    c: DistanceX(g13) = -8
FEATURE [PartDesign::Pocket] Pocket012
  BaseFeature = -> Pocket011
  Length = 0.02
  Length2 = 100
  Profile = -> Sketch036
  Type = 0
FEATURE [PartDesign::Pocket] Pocket013
  BaseFeature = -> Pocket012
  Length = 5
  Length2 = 100
  Profile = -> Sketch033
  Type = 0
FEATURE [PartDesign::Pad] Pad002
  BaseFeature = -> Pocket013
  Direction = (1,1,1)
  Length = 3
  Length2 = 100
  Profile = -> Sketch035
  Reversed = true
  Type = 0
FEATURE [PartDesign::Pocket] Pocket014
  BaseFeature = -> Pad002
  Length = 40
  Length2 = 100
  Profile = -> Sketch037
  Type = 0
FEATURE [PartDesign::Pad] Pad003
  BaseFeature = -> Pocket014
  Direction = (1,1,1)
  Length = 10
  Length2 = 100
  Profile = -> Sketch029
  Type = 0
FEATURE [Sketcher::SketchObject] Sketch039  label="platformBump"
  ExternalGeometry = -> [Pad003]
  FullyConstrained = true
  MapMode = 5
  Support = -> [Pad003]
  sketch-geometry (4):
    g0: LineSegment StartX=-30.6621 StartY=23.5355 StartZ=0 EndX=12.2218 EndY=23.5355 EndZ=0
    g1: LineSegment StartX=12.2218 StartY=23.5355 StartZ=0 EndX=15.7574 EndY=20 EndZ=0
    g2: LineSegment StartX=15.7574 StartY=20 StartZ=0 EndX=-34.1976 EndY=20 EndZ=0
    g3: LineSegment StartX=-34.1976 StartY=20 StartZ=0 EndX=-30.6621 EndY=23.5355 EndZ=0
  constraints (10):
    c: Coincident(g0,g1)
    c: Coincident(g1,g2)
    c: Coincident(g2,g3)
    c: Coincident(g3,g0)
    c: Horizontal(g0)
    c: Distance(g1) = 5
    c: Coincident(g2,g-3)
    c: Coincident(g1,g-4)
    c: Angle(g1) = -0.785398
    c: Angle(g3) = 0.785398
FEATURE [PartDesign::Pad] Pad004
  BaseFeature = -> Pad003
  Direction = (1,1,1)
  Length = 4
  Length2 = 100
  Profile = -> Sketch039
  Reversed = true
  Type = 0
FEATURE [Sketcher::SketchObject] Sketch040  label="WireHoles"
  FullyConstrained = true
  MapMode = 5
  Support = -> [Pad004]
  sketch-geometry (21):
    g0: LineSegment StartX=16.184 StartY=-17.3794 StartZ=0 EndX=17.4696 EndY=-15.8473 EndZ=0
    g1: LineSegment StartX=17.4696 StartY=-15.8473 StartZ=0 EndX=16.7856 EndY=-13.9679 EndZ=0
    g2: LineSegment StartX=16.7856 StartY=-13.9679 StartZ=0 EndX=14.816 EndY=-13.6206 EndZ=0
    g3: LineSegment StartX=14.816 StartY=-13.6206 StartZ=0 EndX=13.5304 EndY=-15.1527 EndZ=0
    g4: LineSegment StartX=13.5304 StartY=-15.1527 StartZ=0 EndX=14.2144 EndY=-17.0321 EndZ=0
    g5: LineSegment StartX=14.2144 StartY=-17.0321 StartZ=0 EndX=16.184 EndY=-17.3794 EndZ=0
    g6: Circle CenterX=15.5 CenterY=-15.5 CenterZ=0 NormalX=0 NormalY=0 NormalZ=1 AngleXU=0 Radius=2
    g7: LineSegment StartX=14.9824 StartY=17.4319 StartZ=0 EndX=13.5681 EndY=16.0176 EndZ=0
    g8: LineSegment StartX=13.5681 StartY=16.0176 StartZ=0 EndX=14.0858 EndY=14.0858 EndZ=0
    g9: LineSegment StartX=14.0858 StartY=14.0858 StartZ=0 EndX=16.0176 EndY=13.5681 EndZ=0
    g10: LineSegment StartX=16.0176 StartY=13.5681 StartZ=0 EndX=17.4319 EndY=14.9824 EndZ=0
    g11: LineSegment StartX=17.4319 StartY=14.9824 StartZ=0 EndX=16.9142 EndY=16.9142 EndZ=0
    g12: LineSegment StartX=16.9142 StartY=16.9142 StartZ=0 EndX=14.9824 EndY=17.4319 EndZ=0
    g13: Circle CenterX=15.5 CenterY=15.5 CenterZ=0 NormalX=0 NormalY=0 NormalZ=1 AngleXU=0 Radius=2
    g14: LineSegment StartX=-14.8333 StartY=-17.1667 StartZ=0 EndX=-14.4062 EndY=-15.5729 EndZ=0
    g15: LineSegment StartX=-14.4062 StartY=-15.5729 StartZ=0 EndX=-15.5729 EndY=-14.4062 EndZ=0
    g16: LineSegment StartX=-15.5729 StartY=-14.4062 StartZ=0 EndX=-17.1667 EndY=-14.8333 EndZ=0
    g17: LineSegment StartX=-17.1667 StartY=-14.8333 StartZ=0 EndX=-17.5938 EndY=-16.4271 EndZ=0
    g18: LineSegment StartX=-17.5938 StartY=-16.4271 StartZ=0 EndX=-16.4271 EndY=-17.5938 EndZ=0
    g19: LineSegment StartX=-16.4271 StartY=-17.5938 StartZ=0 EndX=-14.8333 EndY=-17.1667 EndZ=0
    g20: Circle CenterX=-16 CenterY=-16 CenterZ=0 NormalX=0 NormalY=0 NormalZ=1 AngleXU=0 Radius=1.65
  constraints (51):
    c: Coincident(g0,g1)
    c: Coincident(g1,g2)
    c: Coincident(g2,g3)
    c: Coincident(g3,g4)
    c: Coincident(g4,g5)
    c: Coincident(g5,g0)
    c: Equal(g0, g1-g5) x5
    c: PointOnObject(g0,g6)
    c: PointOnObject(g1,g6)
    c: PointOnObject(g2,g6)
    c: PointOnObject(g3,g6)
    c: PointOnObject(g4,g6)
    c: PointOnObject(g5,g6)
    c: Coincident(g7,g8)
    c: Coincident(g8,g9)
    c: Coincident(g9,g10)
    c: Coincident(g10,g11)
    c: Coincident(g11,g12)
    c: Coincident(g12,g7)
    c: Equal(g7, g8-g12) x5
    c: PointOnObject(g7,g13)
    c: PointOnObject(g8,g13)
    c: PointOnObject(g9,g13)
    c: PointOnObject(g10,g13)
    c: PointOnObject(g11,g13)
    c: PointOnObject(g12,g13)
    c: DistanceX(g13) = 15.5
    c: DistanceY(g13) = 15.5
    c: DistanceX(g6) = 15.5
    c: DistanceY(g6) = -15.5
    c: Coincident(g14,g15)
    c: Coincident(g15,g16)
    c: Coincident(g16,g17)
    c: Coincident(g17,g18)
    c: Coincident(g18,g19)
    c: Coincident(g19,g14)
    c: Equal(g14, g15-g19) x5
    c: PointOnObject(g14,g20)
    c: PointOnObject(g15,g20)
    c: PointOnObject(g16,g20)
    c: PointOnObject(g17,g20)
    c: PointOnObject(g18,g20)
    c: PointOnObject(g19,g20)
    c: Angle(g15) = 2.35619
    c: DistanceX(g20) = -16
    c: DistanceY(g20) = -16
    c: Angle(g3) = -2.26893
    c: Angle(g11) = 1.8326
    c: Diameter(g20) = 3.3
    c: Diameter(g6) = 4
    c: Diameter(g13) = 4
FEATURE [PartDesign::Pocket] Pocket015
  BaseFeature = -> Pad004
  Length = 5
  Length2 = 100
  Profile = -> Sketch040
  Type = 1
FEATURE [Sketcher::SketchObject] Sketch041  label="PCBmountholes"
  FullyConstrained = true
  MapMode = 5
  Placement = pos=(-1.00001,-3.26797e-07,0) rot=(0.57735,0.57735,0.57735;2.0944rad)
  Support = -> [Pocket015]
  sketch-geometry (2):
    g0: Circle CenterX=16 CenterY=-36 CenterZ=0 NormalX=0 NormalY=0 NormalZ=1 AngleXU=0 Radius=1.15
    g1: Circle CenterX=-16 CenterY=-36 CenterZ=0 NormalX=0 NormalY=0 NormalZ=1 AngleXU=0 Radius=1.15
  constraints (5):
    c: Distance(g0,g1) = 32
    c: Symmetric(g1,g0,g-2)
    c: Diameter(g0) = 2.3
    c: Equal(g0,g1)
    c: DistanceY(g1) = -36
FEATURE [Sketcher::SketchObject] Sketch044  label="TopRemove"
  FullyConstrained = false
  MapMode = 5
  Placement = pos=(0,0,0) rot=(1,0,0;1.5708rad)
  Support = -> [XZ_Plane]
  sketch-geometry (4):
    g0: LineSegment StartX=-45.2222 StartY=21.8954 StartZ=0 EndX=42.2472 EndY=21.8954 EndZ=0
    g1: LineSegment StartX=42.2472 StartY=21.8954 StartZ=0 EndX=42.2472 EndY=-8 EndZ=0
    g2: LineSegment StartX=42.2472 StartY=-8 StartZ=0 EndX=-45.2222 EndY=-8 EndZ=0
    g3: LineSegment StartX=-45.2222 StartY=-8 StartZ=0 EndX=-45.2222 EndY=21.8954 EndZ=0
  constraints (9):
    c: Coincident(g0,g1)
    c: Coincident(g1,g2)
    c: Coincident(g2,g3)
    c: Coincident(g3,g0)
    c: Horizontal(g0)
    c: Horizontal(g2)
    c: Vertical(g1)
    c: Vertical(g3)
    c: DistanceY(g1) = -8
FEATURE [Sketcher::SketchObject] Sketch045  label="BottomRemove"
  FullyConstrained = false
  MapMode = 5
  Placement = pos=(0,0,0) rot=(1,0,0;1.5708rad)
  Support = -> [XZ_Plane]
  sketch-geometry (4):
    g0: LineSegment StartX=-38.29 StartY=-24 StartZ=0 EndX=54.8796 EndY=-24 EndZ=0
    g1: LineSegment StartX=54.8796 StartY=-24 StartZ=0 EndX=54.8796 EndY=-80.7262 EndZ=0
    g2: LineSegment StartX=54.8796 StartY=-80.7262 StartZ=0 EndX=-38.29 EndY=-80.7262 EndZ=0
    g3: LineSegment StartX=-38.29 StartY=-80.7262 StartZ=0 EndX=-38.29 EndY=-24 EndZ=0
  constraints (9):
    c: Coincident(g0,g1)
    c: Coincident(g1,g2)
    c: Coincident(g2,g3)
    c: Coincident(g3,g0)
    c: Horizontal(g0)
    c: Horizontal(g2)
    c: Vertical(g1)
    c: Vertical(g3)
    c: DistanceY(g0) = -24
FEATURE [Sketcher::SketchObject] Sketch046  label="TopGenerate"
  FullyConstrained = false
  MapMode = 5
  Placement = pos=(0,0,0) rot=(1,0,0;1.5708rad)
  Support = -> [XZ_Plane]
  sketch-geometry (4):
    g0: LineSegment StartX=-63.8803 StartY=-7.5 StartZ=0 EndX=73.5537 EndY=-7.5 EndZ=0
    g1: LineSegment StartX=73.5537 StartY=-7.5 StartZ=0 EndX=73.5537 EndY=-93.5801 EndZ=0
    g2: LineSegment StartX=73.5537 StartY=-93.5801 StartZ=0 EndX=-63.8803 EndY=-93.5801 EndZ=0
    g3: LineSegment StartX=-63.8803 StartY=-93.5801 StartZ=0 EndX=-63.8803 EndY=-7.5 EndZ=0
  constraints (9):
    c: Coincident(g0,g1)
    c: Coincident(g1,g2)
    c: Coincident(g2,g3)
    c: Coincident(g3,g0)
    c: Horizontal(g0)
    c: Horizontal(g2)
    c: Vertical(g1)
    c: Vertical(g3)
    c: DistanceY(g0) = -7.5
FEATURE [Sketcher::SketchObject] Sketch047  label="BottomGenerat"
  FullyConstrained = false
  MapMode = 5
  Placement = pos=(0,0,0) rot=(1,0,0;1.5708rad)
  Support = -> [XZ_Plane]
  sketch-geometry (4):
    g0: LineSegment StartX=-59.346 StartY=15.5453 StartZ=0 EndX=57.1209 EndY=15.5453 EndZ=0
    g1: LineSegment StartX=57.1209 StartY=15.5453 StartZ=0 EndX=57.1209 EndY=-24.5 EndZ=0
    g2: LineSegment StartX=57.1209 StartY=-24.5 StartZ=0 EndX=-59.346 EndY=-24.5 EndZ=0
    g3: LineSegment StartX=-59.346 StartY=-24.5 StartZ=0 EndX=-59.346 EndY=15.5453 EndZ=0
  constraints (9):
    c: Coincident(g0,g1)
    c: Coincident(g1,g2)
    c: Coincident(g2,g3)
    c: Coincident(g3,g0)
    c: Horizontal(g0)
    c: Horizontal(g2)
    c: Vertical(g1)
    c: Vertical(g3)
    c: DistanceY(g1) = -24.5
FEATURE [PartDesign::Pocket] Pocket016
  BaseFeature = -> Pocket015
  Length = 6
  Length2 = 100
  Profile = -> Sketch041
  Type = 0
FEATURE [Sketcher::SketchObject] Sketch042  label="FilamentBore"
  FullyConstrained = true
  MapMode = 5
  Placement = pos=(0,0,-53) rot=(1,0,0;3.14159rad)
  Support = -> [Pocket016]
  sketch-geometry (7):
    g0: LineSegment StartX=-13.3547 StartY=-12.2 StartZ=0 EndX=-12.7774 EndY=-13.2 EndZ=0
    g1: LineSegment StartX=-12.7774 StartY=-13.2 StartZ=0 EndX=-11.6226 EndY=-13.2 EndZ=0
    g2: LineSegment StartX=-11.6226 StartY=-13.2 StartZ=0 EndX=-11.0453 EndY=-12.2 EndZ=0
    g3: LineSegment StartX=-11.0453 StartY=-12.2 StartZ=0 EndX=-11.6226 EndY=-11.2 EndZ=0
    g4: LineSegment StartX=-11.6226 StartY=-11.2 StartZ=0 EndX=-12.7774 EndY=-11.2 EndZ=0
    g5: LineSegment StartX=-12.7774 StartY=-11.2 StartZ=0 EndX=-13.3547 EndY=-12.2 EndZ=0
    g6: Circle CenterX=-12.2 CenterY=-12.2 CenterZ=0 NormalX=0 NormalY=0 NormalZ=1 AngleXU=0 Radius=1.1547
  constraints (17):
    c: Coincident(g0,g1)
    c: Coincident(g1,g2)
    c: Coincident(g2,g3)
    c: Coincident(g3,g4)
    c: Coincident(g4,g5)
    c: Coincident(g5,g0)
    c: Equal(g0, g1-g5) x5
    c: PointOnObject(g0,g6)
    c: PointOnObject(g1,g6)
    c: PointOnObject(g2,g6)
    c: PointOnObject(g3,g6)
    c: PointOnObject(g4,g6)
    c: PointOnObject(g5,g6)
    c: DistanceX(g6) = -12.2
    c: DistanceY(g6) = -12.2
    c: Distance(g0,g4) = 2
    c: Angle(g1) = 0
FEATURE [PartDesign::Pocket] Pocket017
  BaseFeature = -> Pocket016
  Length = 5
  Length2 = 100
  Profile = -> Sketch042
  Type = 1
FEATURE [Sketcher::SketchObject] Sketch043  label="teflonBore"
  FullyConstrained = true
  MapMode = 5
  Support = -> [Pocket017]
  sketch-geometry (7):
    g0: LineSegment StartX=-10.9587 StartY=10.05 StartZ=0 EndX=-9.71739 EndY=12.2 EndZ=0
    g1: LineSegment StartX=-9.71739 StartY=12.2 StartZ=0 EndX=-10.9587 EndY=14.35 EndZ=0
    g2: LineSegment StartX=-10.9587 StartY=14.35 StartZ=0 EndX=-13.4413 EndY=14.35 EndZ=0
    g3: LineSegment StartX=-13.4413 StartY=14.35 StartZ=0 EndX=-14.6826 EndY=12.2 EndZ=0
    g4: LineSegment StartX=-14.6826 StartY=12.2 StartZ=0 EndX=-13.4413 EndY=10.05 EndZ=0
    g5: LineSegment StartX=-13.4413 StartY=10.05 StartZ=0 EndX=-10.9587 EndY=10.05 EndZ=0
    g6: Circle CenterX=-12.2 CenterY=12.2 CenterZ=0 NormalX=0 NormalY=0 NormalZ=1 AngleXU=0 Radius=2.48261
  constraints (17):
    c: Coincident(g0,g1)
    c: Coincident(g1,g2)
    c: Coincident(g2,g3)
    c: Coincident(g3,g4)
    c: Coincident(g4,g5)
    c: Coincident(g5,g0)
    c: Equal(g0, g1-g5) x5
    c: PointOnObject(g0,g6)
    c: PointOnObject(g1,g6)
    c: PointOnObject(g2,g6)
    c: PointOnObject(g3,g6)
    c: PointOnObject(g4,g6)
    c: PointOnObject(g5,g6)
    c: Horizontal(g2)
    c: DistanceX(g6) = -12.2
    c: DistanceY(g6) = 12.2
    c: Distance(g1,g3) = 4.3
FEATURE [PartDesign::Pocket] Pocket018
  BaseFeature = -> Pocket017
  Length = 37
  Length2 = 100
  Profile = -> Sketch043
  Type = 0
FEATURE [Sketcher::SketchObject] Sketch048  label="TopScrewPilot"
  FullyConstrained = false
  MapMode = 5
  Support = -> [Pocket018]
  sketch-geometry (2):
    g0: Circle CenterX=-15 CenterY=-7.5 CenterZ=0 NormalX=0 NormalY=0 NormalZ=1 AngleXU=0 Radius=1.11214
    g1: Circle CenterX=15 CenterY=7.5 CenterZ=0 NormalX=0 NormalY=0 NormalZ=1 AngleXU=0 Radius=1.10684
  constraints (4):
    c: DistanceY(g1) = 7.5
    c: DistanceX(g1) = 15
    c: DistanceY(g0) = -7.5
    c: DistanceX(g0) = -15
FEATURE [Sketcher::SketchObject] Sketch051  label="TopScrewClearance"
  FullyConstrained = true
  MapMode = 5
  sketch-geometry (14):
    g0: LineSegment StartX=-14.05 StartY=-9.14545 StartZ=0 EndX=-13.1 EndY=-7.5 EndZ=0
    g1: LineSegment StartX=-13.1 StartY=-7.5 StartZ=0 EndX=-14.05 EndY=-5.85455 EndZ=0
    g2: LineSegment StartX=-14.05 StartY=-5.85455 StartZ=0 EndX=-15.95 EndY=-5.85455 EndZ=0
    g3: LineSegment StartX=-15.95 StartY=-5.85455 StartZ=0 EndX=-16.9 EndY=-7.5 EndZ=0
    g4: LineSegment StartX=-16.9 StartY=-7.5 StartZ=0 EndX=-15.95 EndY=-9.14545 EndZ=0
    g5: LineSegment StartX=-15.95 StartY=-9.14545 StartZ=0 EndX=-14.05 EndY=-9.14545 EndZ=0
    g6: Circle CenterX=-15 CenterY=-7.5 CenterZ=0 NormalX=0 NormalY=0 NormalZ=1 AngleXU=0 Radius=1.9
    g7: LineSegment StartX=15.95 StartY=5.85455 StartZ=0 EndX=16.9 EndY=7.5 EndZ=0
    g8: LineSegment StartX=16.9 StartY=7.5 StartZ=0 EndX=15.95 EndY=9.14545 EndZ=0
    g9: LineSegment StartX=15.95 StartY=9.14545 StartZ=0 EndX=14.05 EndY=9.14545 EndZ=0
    g10: LineSegment StartX=14.05 StartY=9.14545 StartZ=0 EndX=13.1 EndY=7.5 EndZ=0
    g11: LineSegment StartX=13.1 StartY=7.5 StartZ=0 EndX=14.05 EndY=5.85455 EndZ=0
    g12: LineSegment StartX=14.05 StartY=5.85455 StartZ=0 EndX=15.95 EndY=5.85455 EndZ=0
    g13: Circle CenterX=15 CenterY=7.5 CenterZ=0 NormalX=0 NormalY=0 NormalZ=1 AngleXU=0 Radius=1.9
  constraints (34):
    c: Coincident(g0,g1)
    c: Coincident(g1,g2)
    c: Coincident(g2,g3)
    c: Coincident(g3,g4)
    c: Coincident(g4,g5)
    c: Coincident(g5,g0)
    c: Equal(g0, g1-g5) x5
    c: PointOnObject(g0,g6)
    c: PointOnObject(g1,g6)
    c: PointOnObject(g2,g6)
    c: PointOnObject(g3,g6)
    c: PointOnObject(g4,g6)
    c: PointOnObject(g5,g6)
    c: Coincident(g7,g8)
    c: Coincident(g8,g9)
    c: Coincident(g9,g10)
    c: Coincident(g10,g11)
    c: Coincident(g11,g12)
    c: Coincident(g12,g7)
    c: Equal(g7, g8-g12) x5
    c: PointOnObject(g7,g13)
    c: PointOnObject(g8,g13)
    c: PointOnObject(g9,g13)
    c: PointOnObject(g10,g13)
    c: PointOnObject(g11,g13)
    c: PointOnObject(g12,g13)
    c: DistanceX(g13) = 15
    c: DistanceX(g6) = -15
    c: Diameter(g6) = 3.8
    c: Diameter(g13) = 3.8
    c: Horizontal(g2)
    c: Horizontal(g9)
    c: DistanceY(g6) = -7.5
    c: DistanceY(g13) = 7.5
FEATURE [PartDesign::Pocket] Pocket019
  BaseFeature = -> Pocket018
  Length = 15
  Length2 = 100
  Profile = -> Sketch048
  Type = 0
FEATURE [Sketcher::SketchObject] Sketch050  label="TopScrewHeatsink"
  FullyConstrained = true
  MapMode = 5
  Placement = pos=(0,0,-15) rot=(0,0,1;0rad)
  Support = -> [Pocket019]
  sketch-geometry (14):
    g0: LineSegment StartX=16.25 StartY=5.33494 StartZ=0 EndX=17.5 EndY=7.5 EndZ=0
    g1: LineSegment StartX=17.5 StartY=7.5 StartZ=0 EndX=16.25 EndY=9.66506 EndZ=0
    g2: LineSegment StartX=16.25 StartY=9.66506 StartZ=0 EndX=13.75 EndY=9.66506 EndZ=0
    g3: LineSegment StartX=13.75 StartY=9.66506 StartZ=0 EndX=12.5 EndY=7.5 EndZ=0
    g4: LineSegment StartX=12.5 StartY=7.5 StartZ=0 EndX=13.75 EndY=5.33494 EndZ=0
    g5: LineSegment StartX=13.75 StartY=5.33494 StartZ=0 EndX=16.25 EndY=5.33494 EndZ=0
    g6: Circle CenterX=15 CenterY=7.5 CenterZ=0 NormalX=0 NormalY=0 NormalZ=1 AngleXU=0 Radius=2.5
    g7: LineSegment StartX=-12.5 StartY=-7.5 StartZ=0 EndX=-13.75 EndY=-5.33494 EndZ=0
    g8: LineSegment StartX=-13.75 StartY=-5.33494 StartZ=0 EndX=-16.25 EndY=-5.33494 EndZ=0
    g9: LineSegment StartX=-16.25 StartY=-5.33494 StartZ=0 EndX=-17.5 EndY=-7.5 EndZ=0
    g10: LineSegment StartX=-17.5 StartY=-7.5 StartZ=0 EndX=-16.25 EndY=-9.66506 EndZ=0
    g11: LineSegment StartX=-16.25 StartY=-9.66506 StartZ=0 EndX=-13.75 EndY=-9.66506 EndZ=0
    g12: LineSegment StartX=-13.75 StartY=-9.66506 StartZ=0 EndX=-12.5 EndY=-7.5 EndZ=0
    g13: Circle CenterX=-15 CenterY=-7.5 CenterZ=0 NormalX=0 NormalY=0 NormalZ=1 AngleXU=0 Radius=2.5
  constraints (34):
    c: Coincident(g0,g1)
    c: Coincident(g1,g2)
    c: Coincident(g2,g3)
    c: Coincident(g3,g4)
    c: Coincident(g4,g5)
    c: Coincident(g5,g0)
    c: Equal(g0, g1-g5) x5
    c: PointOnObject(g0,g6)
    c: PointOnObject(g1,g6)
    c: PointOnObject(g2,g6)
    c: PointOnObject(g3,g6)
    c: PointOnObject(g4,g6)
    c: PointOnObject(g5,g6)
    c: Coincident(g7,g8)
    c: Coincident(g8,g9)
    c: Coincident(g9,g10)
    c: Coincident(g10,g11)
    c: Coincident(g11,g12)
    c: Coincident(g12,g7)
    c: Equal(g7, g8-g12) x5
    c: PointOnObject(g7,g13)
    c: PointOnObject(g8,g13)
    c: PointOnObject(g9,g13)
    c: PointOnObject(g10,g13)
    c: PointOnObject(g11,g13)
    c: PointOnObject(g12,g13)
    c: Equal(g13,g6)
    c: Horizontal(g2)
    c: Horizontal(g8)
    c: DistanceX(g6) = 15
    c: DistanceX(g13) = -15
    c: DistanceY(g6) = 7.5
    c: DistanceY(g13) = -7.5
    c: Diameter(g13) = 5
FEATURE [PartDesign::Pocket] Pocket020
  BaseFeature = -> Pocket019
  Length = 8
  Length2 = 100
  Profile = -> Sketch050
  Reversed = true
  Type = 0
FEATURE [PartDesign::Pocket] Pocket021
  BaseFeature = -> Pocket020
  Length = 8
  Length2 = 100
  Profile = -> Sketch051
  Type = 0
FEATURE [Sketcher::SketchObject] Sketch053
  FullyConstrained = true
  MapMode = 5
  Placement = pos=(0,0,-32) rot=(1,0,0;3.14159rad)
  Support = -> [Pocket021]
  sketch-geometry (15):
    g0: LineSegment StartX=3.39545 StartY=14.05 StartZ=0 EndX=3.39545 EndY=15.95 EndZ=0
    g1: LineSegment StartX=3.39545 StartY=15.95 StartZ=0 EndX=1.75 EndY=16.9 EndZ=0
    g2: LineSegment StartX=1.75 StartY=16.9 StartZ=0 EndX=0.104552 EndY=15.95 EndZ=0
    g3: LineSegment StartX=0.104552 StartY=15.95 StartZ=0 EndX=0.104552 EndY=14.05 EndZ=0
    g4: LineSegment StartX=0.104552 StartY=14.05 StartZ=0 EndX=1.75 EndY=13.1 EndZ=0
    g5: LineSegment StartX=1.75 StartY=13.1 StartZ=0 EndX=3.39545 EndY=14.05 EndZ=0
    g6: Circle CenterX=1.75 CenterY=15 CenterZ=0 NormalX=0 NormalY=0 NormalZ=1 AngleXU=0 Radius=1.9
    g7: LineSegment StartX=1.75 StartY=-16.9 StartZ=0 EndX=3.39545 EndY=-15.95 EndZ=0
    g8: LineSegment StartX=3.39545 StartY=-15.95 StartZ=0 EndX=3.39545 EndY=-14.05 EndZ=0
    g9: LineSegment StartX=3.39545 StartY=-14.05 StartZ=0 EndX=1.75 EndY=-13.1 EndZ=0
    g10: LineSegment StartX=1.75 StartY=-13.1 StartZ=0 EndX=0.104552 EndY=-14.05 EndZ=0
    g11: LineSegment StartX=0.104552 StartY=-14.05 StartZ=0 EndX=0.104552 EndY=-15.95 EndZ=0
    g12: LineSegment StartX=0.104552 StartY=-15.95 StartZ=0 EndX=1.75 EndY=-16.9 EndZ=0
    g13: Circle CenterX=1.75 CenterY=-15 CenterZ=0 NormalX=0 NormalY=0 NormalZ=1 AngleXU=0 Radius=1.9
    g14: Circle CenterX=1.75 CenterY=15 CenterZ=0 NormalX=0 NormalY=0 NormalZ=1 AngleXU=0 Radius=2.5
  constraints (36):
    c: Coincident(g0,g1)
    c: Coincident(g1,g2)
    c: Coincident(g2,g3)
    c: Coincident(g3,g4)
    c: Coincident(g4,g5)
    c: Coincident(g5,g0)
    c: Equal(g0, g1-g5) x5
    c: PointOnObject(g0,g6)
    c: PointOnObject(g1,g6)
    c: PointOnObject(g2,g6)
    c: PointOnObject(g3,g6)
    c: PointOnObject(g4,g6)
    c: PointOnObject(g5,g6)
    c: Coincident(g7,g8)
    c: Coincident(g8,g9)
    c: Coincident(g9,g10)
    c: Coincident(g10,g11)
    c: Coincident(g11,g12)
    c: Coincident(g12,g7)
    c: Equal(g7, g8-g12) x5
    c: PointOnObject(g7,g13)
    c: PointOnObject(g8,g13)
    c: PointOnObject(g9,g13)
    c: PointOnObject(g10,g13)
    c: PointOnObject(g11,g13)
    c: PointOnObject(g12,g13)
    c: DistanceY(g13) = -15
    c: DistanceY(g6) = 15
    c: Vertical(g3)
    c: Vertical(g11)
    c: Diameter(g13) = 3.8
    c: Equal(g13,g6)
    c: Coincident(g14,g6)
    c: Diameter(g14) = 5
    c: DistanceX(g6) = 1.75
    c: DistanceX(g13) = 1.75
FEATURE [PartDesign::Pocket] Pocket022
  BaseFeature = -> Pocket021
  Length = 16.5
  Length2 = 100
  Profile = -> Sketch053
  Type = 0
FEATURE [Sketcher::SketchObject] Sketch054
  FullyConstrained = true
  MapMode = 5
  Placement = pos=(0,-3.7e-15,-16.7) rot=(0,0,1;0rad)
  Support = -> [Pocket022]
  sketch-geometry (14):
    g0: LineSegment StartX=3.65526 StartY=-16.1 StartZ=0 EndX=3.65526 EndY=-13.9 EndZ=0
    g1: LineSegment StartX=3.65526 StartY=-13.9 StartZ=0 EndX=1.75 EndY=-12.8 EndZ=0
    g2: LineSegment StartX=1.75 StartY=-12.8 StartZ=0 EndX=-0.155256 EndY=-13.9 EndZ=0
    g3: LineSegment StartX=-0.155256 StartY=-13.9 StartZ=0 EndX=-0.155256 EndY=-16.1 EndZ=0
    g4: LineSegment StartX=-0.155256 StartY=-16.1 StartZ=0 EndX=1.75 EndY=-17.2 EndZ=0
    g5: LineSegment StartX=1.75 StartY=-17.2 StartZ=0 EndX=3.65526 EndY=-16.1 EndZ=0
    g6: Circle CenterX=1.75 CenterY=-15 CenterZ=0 NormalX=0 NormalY=0 NormalZ=1 AngleXU=0 Radius=2.2
    g7: LineSegment StartX=3.65526 StartY=13.9 StartZ=0 EndX=3.65526 EndY=16.1 EndZ=0
    g8: LineSegment StartX=3.65526 StartY=16.1 StartZ=0 EndX=1.75 EndY=17.2 EndZ=0
    g9: LineSegment StartX=1.75 StartY=17.2 StartZ=0 EndX=-0.155256 EndY=16.1 EndZ=0
    g10: LineSegment StartX=-0.155256 StartY=16.1 StartZ=0 EndX=-0.155256 EndY=13.9 EndZ=0
    g11: LineSegment StartX=-0.155256 StartY=13.9 StartZ=0 EndX=1.75 EndY=12.8 EndZ=0
    g12: LineSegment StartX=1.75 StartY=12.8 StartZ=0 EndX=3.65526 EndY=13.9 EndZ=0
    g13: Circle CenterX=1.75 CenterY=15 CenterZ=0 NormalX=0 NormalY=0 NormalZ=1 AngleXU=0 Radius=2.2
  constraints (34):
    c: Coincident(g0,g1)
    c: Coincident(g1,g2)
    c: Coincident(g2,g3)
    c: Coincident(g3,g4)
    c: Coincident(g4,g5)
    c: Coincident(g5,g0)
    c: Equal(g0, g1-g5) x5
    c: PointOnObject(g0,g6)
    c: PointOnObject(g1,g6)
    c: PointOnObject(g2,g6)
    c: PointOnObject(g3,g6)
    c: PointOnObject(g4,g6)
    c: PointOnObject(g5,g6)
    c: Coincident(g7,g8)
    c: Coincident(g8,g9)
    c: Coincident(g9,g10)
    c: Coincident(g10,g11)
    c: Coincident(g11,g12)
    c: Coincident(g12,g7)
    c: Equal(g7, g8-g12) x5
    c: PointOnObject(g7,g13)
    c: PointOnObject(g8,g13)
    c: PointOnObject(g9,g13)
    c: PointOnObject(g10,g13)
    c: PointOnObject(g11,g13)
    c: PointOnObject(g12,g13)
    c: Vertical(g7)
    c: Vertical(g0)
    c: DistanceY(g6) = -15
    c: DistanceY(g13) = 15
    c: DistanceX(g13) = 1.75
    c: DistanceX(g6) = 1.75
    c: Diameter(g6) = 4.4
    c: Equal(g6,g13)
FEATURE [PartDesign::Pocket] Pocket023
  BaseFeature = -> Pocket022
  Length = 8
  Length2 = 100
  Profile = -> Sketch054
  Type = 0
FEATURE [PartDesign::Body] Body
  Group = -> [Sketch,Pad,Sketch001,Pocket,Sketch003,Sketch004,Sketch007,Sketch008,Sketch009,Sketch010,Sketch017,Sketch019,Sketch021,Pocket002,Sketch022,Sketch024,Sketch025,Sketch026,Pocket003,Pocket004,Pocket005,Pocket006,Pocket007,Pocket008,Pad001,Pocket009,Pocket010,Sketch029,Sketch033,Sketch035,Sketch036,Sketch037,Pocket011,Pocket012,Pocket013,Pad002,Pocket014,Pad003,Sketch039,Pad004,Sketch040,Pocket015,+20 more]
  Origin = -> Origin
  Placement = pos=(0,0,0) rot=(0.862856,-0.357407,0.357407;1.71777rad)
  Tip = -> Pocket023
FEATURE [Mesh::Feature] Mesh  label="Pocket025 (Meshed)"
FEATURE [Mesh::Feature] Mesh001  label="Pocket024 (Meshed)"
FEATURE [Mesh::Feature] Mesh002  label="Pocket024 (Meshed)001"
